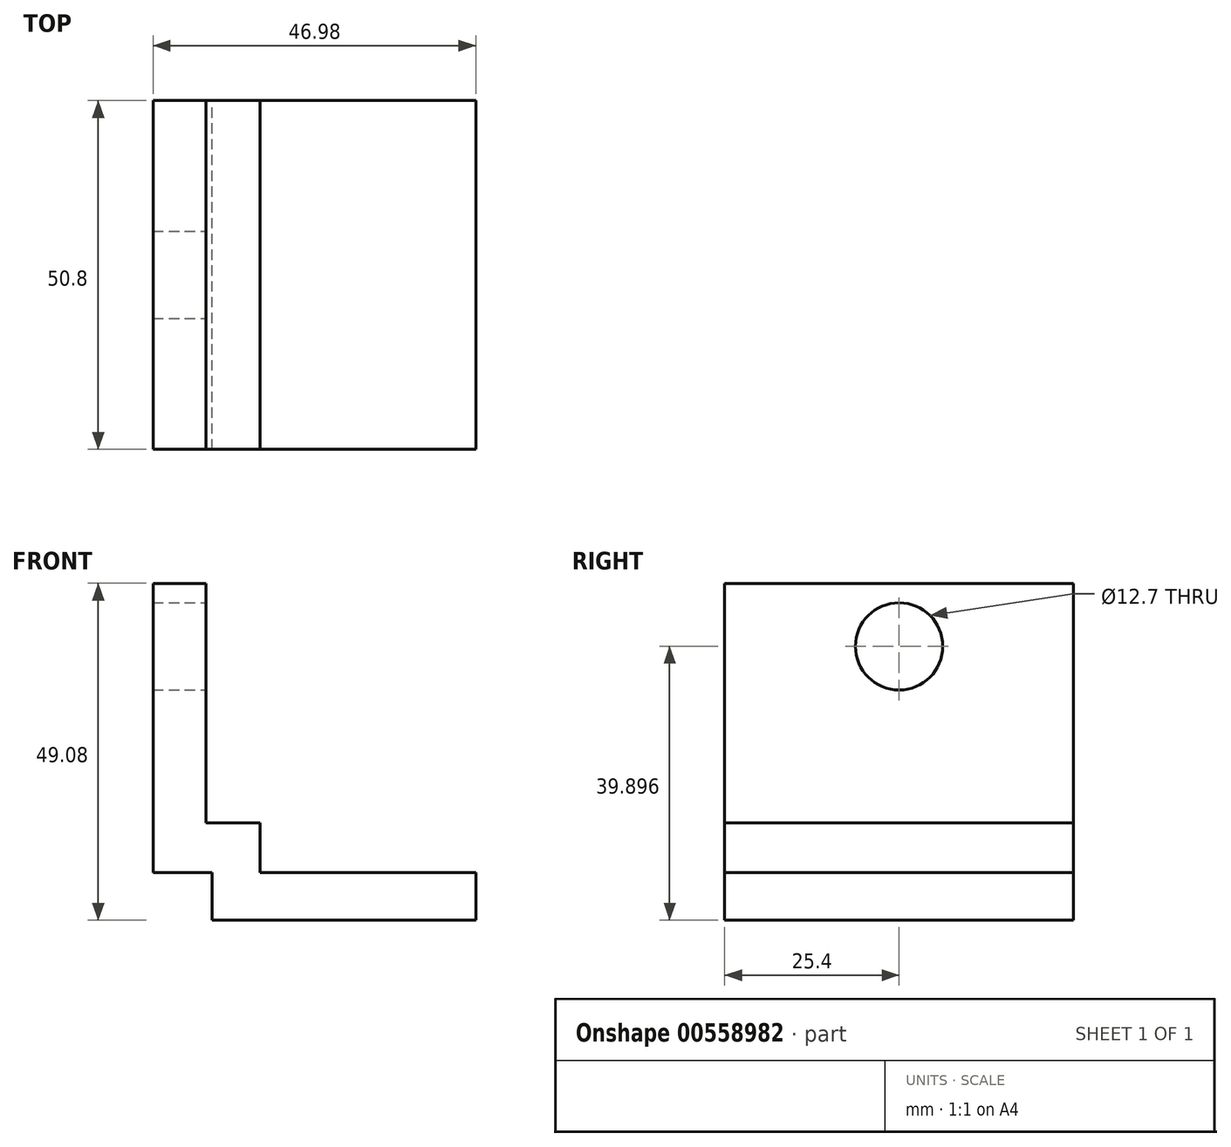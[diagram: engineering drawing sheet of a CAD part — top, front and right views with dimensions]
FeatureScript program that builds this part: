
annotation { "Feature Type Name" : "Feature", "Feature Type Description" : "" }
export const myFeature = defineFeature(function(context is Context, id is Id, definition is map)
    precondition{}
    {
        {
            var Q0;
            Q0=qCreatedBy(makeId("Front.planeOp"),FACE);
            var sketch = newSketch(context, id + "F0", { "sketchPlane" : qUnion([Q0])});
            skLineSegment(sketch, "E0", {"start": v(0, 49.08) * mm, "end": v(0, 6.98) * mm});
            skLineSegment(sketch, "E1", {"start": v(0, 6.98) * mm, "end": v(8.6, 6.98) * mm});
            skLineSegment(sketch, "E2", {"start": v(8.6, 6.98) * mm, "end": v(8.6, 0) * mm});
            skLineSegment(sketch, "E3", {"start": v(8.6, 0) * mm, "end": v(46.98, 0) * mm});
            skLineSegment(sketch, "E4", {"start": v(46.98, 0) * mm, "end": v(46.98, 6.98) * mm});
            skLineSegment(sketch, "E5", {"start": v(46.98, 6.98) * mm, "end": v(15.58, 6.98) * mm});
            skLineSegment(sketch, "E6", {"start": v(15.58, 6.98) * mm, "end": v(15.58, 14.19) * mm});
            skLineSegment(sketch, "E7", {"start": v(15.58, 14.19) * mm, "end": v(7.68, 14.19) * mm});
            skLineSegment(sketch, "E8", {"start": v(7.68, 14.19) * mm, "end": v(7.68, 49.08) * mm});
            skLineSegment(sketch, "E9", {"start": v(7.68, 49.08) * mm, "end": v(0, 49.08) * mm});
            skSolve(sketch);
        }
        {
            var Q0;
            Q0=makeQuery(id+"F0.imprint","IMPRINT",FACE,{"disambiguationData":[TD([[makeQuery(id+"F0.imprint","IMPRINT",EDGE,{"derivedFrom":sQuery(id+"F0.wireOp",EDGE,"E0")}),1.0]])]});
            extrude(context, id + "F1", {"entities" : qUnion([Q0]), "depth" : 50.8 * mm, "offsetDistance" : 25.4 * mm});
        }
        {
            var Q0;
            Q0=makeQuery(id+"F1.opExtrude","SWEPT_FACE",FACE,{"disambiguationData":[OSD([sQuery(id+"F0.wireOp",EDGE,"E8")])]});
            var sketch = newSketch(context, id + "F2", { "sketchPlane" : qUnion([Q0])});
            skCircle(sketch, "E10", {"center": v(-25.4, 39.9) * mm, "radius": 5.28 * mm});
            skPoint(sketch, "E10.centerSnap0", {"position": v(-25.4, 49.08) * mm});
            skCircle(sketch, "E11", {"center": v(-41.38, 22.47) * mm, "radius": 5.63 * mm});
            skCircle(sketch, "E12.MirrorC", {"center": v(-9.42, 22.47) * mm, "radius": 5.63 * mm});
            skPoint(sketch, "E13.orphan", {"position": v(-25.4, 14.19) * mm});
            skSolve(sketch);
        }
        {
            var Q0;
            Q0=sQuery(id+"F2.wireOp",VERTEX,"E10.center");
            var Q1;
            Q1=makeQuery(id+"F1.opExtrude","SWEPT_BODY",BODY,{"disambiguationData":[OSD([sQuery(id+"F0.wireOp",EDGE,"E0"),sQuery(id+"F0.wireOp",EDGE,"E1"),sQuery(id+"F0.wireOp",EDGE,"E2"),sQuery(id+"F0.wireOp",EDGE,"E3"),sQuery(id+"F0.wireOp",EDGE,"E4"),sQuery(id+"F0.wireOp",EDGE,"E5"),sQuery(id+"F0.wireOp",EDGE,"E6"),sQuery(id+"F0.wireOp",EDGE,"E7"),sQuery(id+"F0.wireOp",EDGE,"E8"),sQuery(id+"F0.wireOp",EDGE,"E9")])]});
            hole(context, id + "F3", {"style" : HoleStyle.SIMPLE, "endStyle" : HoleEndStyle.THROUGH, "holeDiameter" : 12.7 * mm, "majorDiameter" : 6.35 * mm, "isTappedThrough" : true, "tappedDepth" : 12.7 * mm, "tapClearance" : 3, "locations" : qUnion([Q0]), "scope" : qUnion([Q1])});
        }
    });
